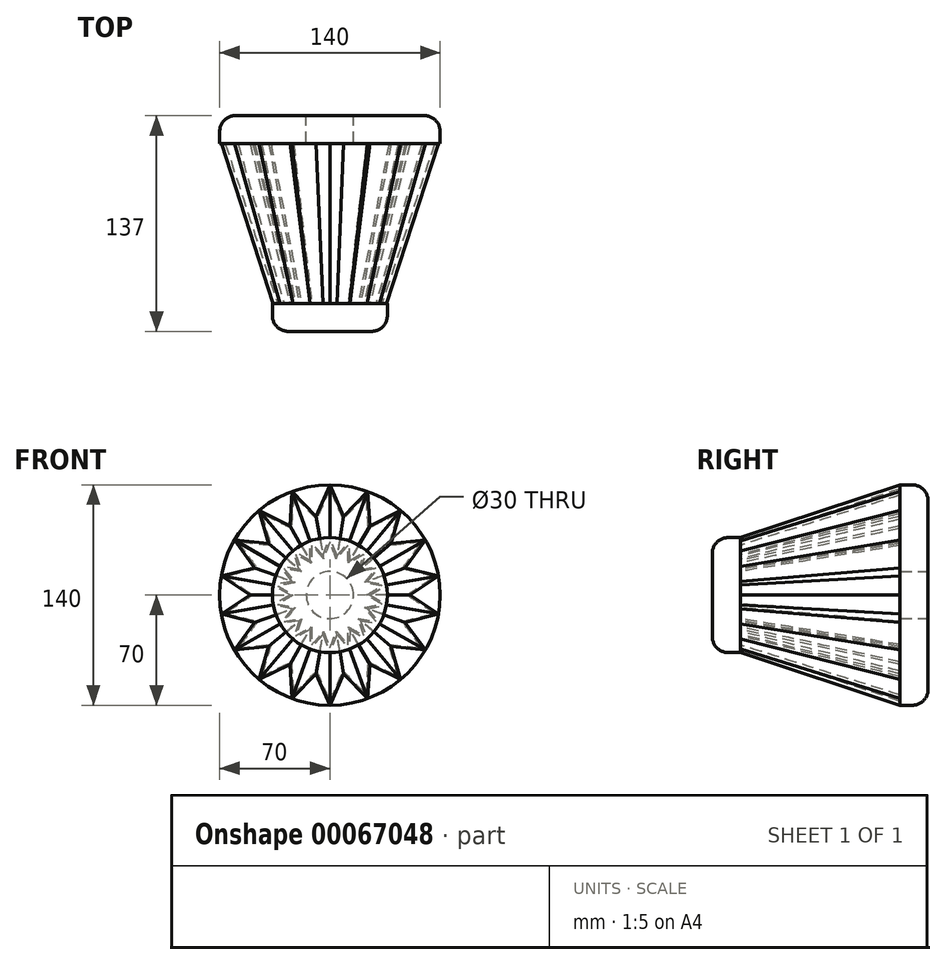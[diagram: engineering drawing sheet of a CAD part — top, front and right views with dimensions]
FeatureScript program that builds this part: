
annotation { "Feature Type Name" : "Feature", "Feature Type Description" : "" }
export const myFeature = defineFeature(function(context is Context, id is Id, definition is map)
    precondition{}
    {
        {
            var Q0;
            Q0=qCreatedBy(makeId("Front.planeOp"),FACE);
            var sketch = newSketch(context, id + "F0", { "sketchPlane" : qUnion([Q0])});
            skLineSegment(sketch, "E0", {"start": v(0, 70) * mm, "end": v(0, 0) * mm, "construction": true});
            skLineSegment(sketch, "E1", {"start": v(0, 70) * mm, "end": v(-8.82, 50) * mm});
            skLineSegment(sketch, "E2", {"start": v(-8.82, 50) * mm, "end": v(0, 0) * mm});
            skLineSegment(sketch, "E3.MirrorCS", {"start": v(0, 70) * mm, "end": v(8.82, 50) * mm});
            skLineSegment(sketch, "E4.MirrorCS", {"start": v(8.82, 50) * mm, "end": v(0, 0) * mm});
            skSolve(sketch);
        }
        {
            var Q0;
            Q0=qCreatedBy(makeId("Front.planeOp"),FACE);
            cPlane(context, id + "F1", {"entities" : qUnion([Q0]), "cplaneType" : CPlaneType.OFFSET, "offset" : 101.5 * mm, "width" : 152.4 * mm, "height" : 152.4 * mm});
        }
        {
            var Q0;
            Q0=qCreatedBy(id+"F1.planeOp",FACE);
            var sketch = newSketch(context, id + "F2", { "sketchPlane" : qUnion([Q0])});
            skLineSegment(sketch, "E5", {"start": v(0, 0) * mm, "end": v(0, 70) * mm, "construction": true});
            skLineSegment(sketch, "E6", {"start": v(0, 0) * mm, "end": v(-4.4, 25) * mm});
            skLineSegment(sketch, "E7", {"start": v(-4.4, 25) * mm, "end": v(0, 36.5) * mm});
            skLineSegment(sketch, "E8.MirrorCS", {"start": v(4.4, 25) * mm, "end": v(0, 36.5) * mm});
            skLineSegment(sketch, "E9.MirrorCS", {"start": v(0, 0) * mm, "end": v(4.4, 25) * mm});
            skSolve(sketch);
        }
        {
            var Q0;
            Q0=qSketchRegion(id+"F0",true);
            var Q1;
            Q1=qSketchRegion(id+"F2",true);
            loft(context, id + "F3", {"sheetProfilesArray" : [{ "sheetProfileEntities" : qUnion([Q0]) }, { "sheetProfileEntities" : qUnion([Q1]) }]});
        }
        {
            var Q0;
            Q0=makeQuery(id+"F3.opLoft","SWEPT_BODY",BODY,{"disambiguationData":[OSD([makeQuery(id+"F0.imprint","IMPRINT",FACE,{"disambiguationData":[TD([[makeQuery(id+"F0.imprint","IMPRINT",EDGE,{"derivedFrom":sQuery(id+"F0.wireOp",EDGE,"E1")}),1.0]])]}),makeQuery(id+"F2.imprint","IMPRINT",FACE,{"disambiguationData":[TD([[makeQuery(id+"F2.imprint","IMPRINT",EDGE,{"derivedFrom":sQuery(id+"F2.wireOp",EDGE,"E6")}),-1.0]])]})])]});
            var Q1;
            Q1=makeQuery(id+"F3.opLoft","SWEPT_EDGE",EDGE,{"disambiguationData":[OSD([sQuery(id+"F0.wireOp",EDGE,"E2"),sQuery(id+"F0.wireOp",EDGE,"E4.MirrorCS"),sQuery(id+"F2.wireOp",EDGE,"E6"),sQuery(id+"F2.wireOp",EDGE,"E9.MirrorCS")])]});
            circularPattern(context, id + "F4", {"operationType" : NewBodyOperationType.ADD, "entities" : qUnion([Q0]), "axis" : qUnion([Q1]), "angle" : 360 * degree, "instanceCount" : round(18), "equalSpace" : true});
        }
        {
            var Q0;
            {var subQ0=makeQuery(id+"F3.opLoft","CAP_FACE",FACE,{"disambiguationData":[OSD([makeQuery(id+"F0.imprint","IMPRINT",FACE,{"disambiguationData":[TD([[makeQuery(id+"F0.imprint","IMPRINT",EDGE,{"derivedFrom":sQuery(id+"F0.wireOp",EDGE,"E1")}),1.0]])]})])],"isStart":true});Q0=makeQuery(id+"F4.boolean.opBoolean","MERGE",FACE,{"derivedFrom":[subQ0,makeQuery(id+"F4.opPattern","COPY",FACE,{"derivedFrom":subQ0,"instanceName":"1"}),makeQuery(id+"F4.opPattern","COPY",FACE,{"derivedFrom":subQ0,"instanceName":"2"}),makeQuery(id+"F4.opPattern","COPY",FACE,{"derivedFrom":subQ0,"instanceName":"3"}),makeQuery(id+"F4.opPattern","COPY",FACE,{"derivedFrom":subQ0,"instanceName":"4"}),makeQuery(id+"F4.opPattern","COPY",FACE,{"derivedFrom":subQ0,"instanceName":"5"}),makeQuery(id+"F4.opPattern","COPY",FACE,{"derivedFrom":subQ0,"instanceName":"6"}),makeQuery(id+"F4.opPattern","COPY",FACE,{"derivedFrom":subQ0,"instanceName":"7"}),makeQuery(id+"F4.opPattern","COPY",FACE,{"derivedFrom":subQ0,"instanceName":"8"}),makeQuery(id+"F4.opPattern","COPY",FACE,{"derivedFrom":subQ0,"instanceName":"9"}),makeQuery(id+"F4.opPattern","COPY",FACE,{"derivedFrom":subQ0,"instanceName":"10"}),makeQuery(id+"F4.opPattern","COPY",FACE,{"derivedFrom":subQ0,"instanceName":"11"}),makeQuery(id+"F4.opPattern","COPY",FACE,{"derivedFrom":subQ0,"instanceName":"12"}),makeQuery(id+"F4.opPattern","COPY",FACE,{"derivedFrom":subQ0,"instanceName":"13"}),makeQuery(id+"F4.opPattern","COPY",FACE,{"derivedFrom":subQ0,"instanceName":"14"}),makeQuery(id+"F4.opPattern","COPY",FACE,{"derivedFrom":subQ0,"instanceName":"15"}),makeQuery(id+"F4.opPattern","COPY",FACE,{"derivedFrom":subQ0,"instanceName":"16"}),makeQuery(id+"F4.opPattern","COPY",FACE,{"derivedFrom":subQ0,"instanceName":"17"})]});}
            var Q1;
            {var subQ0=makeQuery(id+"F3.opLoft","CAP_FACE",FACE,{"disambiguationData":[OSD([makeQuery(id+"F2.imprint","IMPRINT",FACE,{"disambiguationData":[TD([[makeQuery(id+"F2.imprint","IMPRINT",EDGE,{"derivedFrom":sQuery(id+"F2.wireOp",EDGE,"E6")}),-1.0]])]})])],"isStart":true});Q1=makeQuery(id+"F4.boolean.opBoolean","MERGE",FACE,{"derivedFrom":[subQ0,makeQuery(id+"F4.opPattern","COPY",FACE,{"derivedFrom":subQ0,"instanceName":"1"}),makeQuery(id+"F4.opPattern","COPY",FACE,{"derivedFrom":subQ0,"instanceName":"2"}),makeQuery(id+"F4.opPattern","COPY",FACE,{"derivedFrom":subQ0,"instanceName":"3"}),makeQuery(id+"F4.opPattern","COPY",FACE,{"derivedFrom":subQ0,"instanceName":"4"}),makeQuery(id+"F4.opPattern","COPY",FACE,{"derivedFrom":subQ0,"instanceName":"5"}),makeQuery(id+"F4.opPattern","COPY",FACE,{"derivedFrom":subQ0,"instanceName":"6"}),makeQuery(id+"F4.opPattern","COPY",FACE,{"derivedFrom":subQ0,"instanceName":"7"}),makeQuery(id+"F4.opPattern","COPY",FACE,{"derivedFrom":subQ0,"instanceName":"8"}),makeQuery(id+"F4.opPattern","COPY",FACE,{"derivedFrom":subQ0,"instanceName":"9"}),makeQuery(id+"F4.opPattern","COPY",FACE,{"derivedFrom":subQ0,"instanceName":"10"}),makeQuery(id+"F4.opPattern","COPY",FACE,{"derivedFrom":subQ0,"instanceName":"11"}),makeQuery(id+"F4.opPattern","COPY",FACE,{"derivedFrom":subQ0,"instanceName":"12"}),makeQuery(id+"F4.opPattern","COPY",FACE,{"derivedFrom":subQ0,"instanceName":"13"}),makeQuery(id+"F4.opPattern","COPY",FACE,{"derivedFrom":subQ0,"instanceName":"14"}),makeQuery(id+"F4.opPattern","COPY",FACE,{"derivedFrom":subQ0,"instanceName":"15"}),makeQuery(id+"F4.opPattern","COPY",FACE,{"derivedFrom":subQ0,"instanceName":"16"}),makeQuery(id+"F4.opPattern","COPY",FACE,{"derivedFrom":subQ0,"instanceName":"17"})]});}
            shell(context, id + "F5", {"entities" : qUnion([Q0, Q1]), "thickness" : 1 * mm});
        }
        {
            var Q0;
            Q0=qCreatedBy(makeId("Front.planeOp"),FACE);
            var sketch = newSketch(context, id + "F6", { "sketchPlane" : qUnion([Q0])});
            skCircle(sketch, "E10", {"center": v(0, 0) * mm, "radius": 70 * mm});
            skSolve(sketch);
        }
        {
            var Q0;
            Q0=qSketchRegion(id+"F6",true);
            extrude(context, id + "F7", {"entities" : qUnion([Q0]), "oppositeDirection" : true, "depth" : 17.75 * mm});
        }
        {
            var Q0;
            Q0=qCreatedBy(id+"F1.planeOp",FACE);
            var sketch = newSketch(context, id + "F8", { "sketchPlane" : qUnion([Q0])});
            skCircle(sketch, "E11", {"center": v(0, 0) * mm, "radius": 36.5 * mm});
            skSolve(sketch);
        }
        {
            var Q0;
            Q0=qSketchRegion(id+"F8",true);
            extrude(context, id + "F9", {"entities" : qUnion([Q0]), "depth" : 17.75 * mm});
        }
        {
            var Q0;
            Q0=makeQuery(id+"F9.opExtrude","CAP_EDGE",EDGE,{"disambiguationData":[OSD([sQuery(id+"F8.wireOp",EDGE,"E11")])],"isStart":false});
            var Q1;
            Q1=makeQuery(id+"F7.opExtrude","CAP_EDGE",EDGE,{"disambiguationData":[OSD([sQuery(id+"F6.wireOp",EDGE,"E10")])],"isStart":false});
            fillet(context, id + "F10", {"entities" : qUnion([Q0, Q1]), "radius" : 10 * mm, "tangentPropagation" : true, "allowEdgeOverflow" : false});
        }
        {
            var Q0;
            Q0=makeQuery(id+"F7.opExtrude","CAP_FACE",FACE,{"disambiguationData":[OSD([sQuery(id+"F6.wireOp",EDGE,"E10")])],"isStart":false});
            var sketch = newSketch(context, id + "F11", { "sketchPlane" : qUnion([Q0])});
            skCircle(sketch, "E12", {"center": v(0, 0) * mm, "radius": 15 * mm});
            skSolve(sketch);
        }
        {
            var Q0;
            Q0=qSketchRegion(id+"F11",true);
            extrude(context, id + "F12", {"entities" : qUnion([Q0]), "operationType" : NewBodyOperationType.REMOVE, "oppositeDirection" : true, "depth" : 17.75 * mm});
        }
    });
